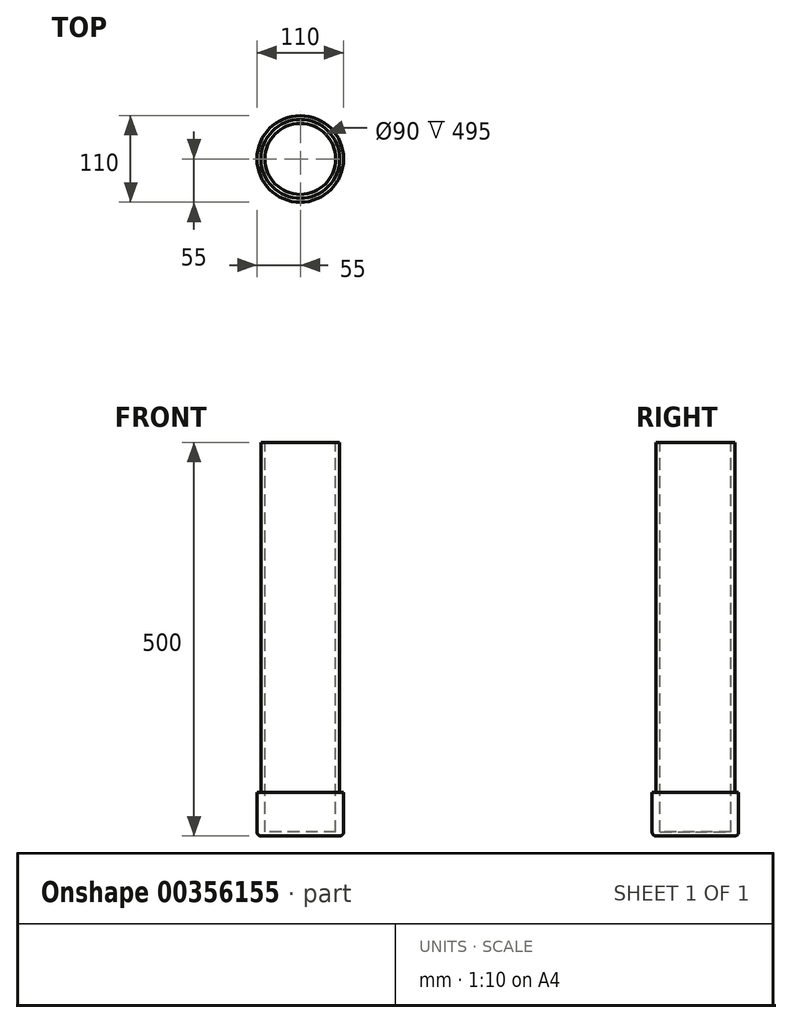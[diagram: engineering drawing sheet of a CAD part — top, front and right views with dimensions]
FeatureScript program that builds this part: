
annotation { "Feature Type Name" : "Feature", "Feature Type Description" : "" }
export const myFeature = defineFeature(function(context is Context, id is Id, definition is map)
    precondition{}
    {
        {
            var Q0;
            Q0=qCreatedBy(makeId("Front.planeOp"),FACE);
            var sketch = newSketch(context, id + "F0", { "sketchPlane" : qUnion([Q0])});
            skLineSegment(sketch, "E0.bottom", {"start": v(0, 0) * mm, "end": v(-50, 0) * mm});
            skLineSegment(sketch, "E0.top", {"start": v(0, 500) * mm, "end": v(-50, 500) * mm});
            skLineSegment(sketch, "E0.left", {"start": v(0, 0) * mm, "end": v(0, 500) * mm});
            skLineSegment(sketch, "E0.right", {"start": v(-50, 0) * mm, "end": v(-50, 500) * mm});
            skLineSegment(sketch, "E1.bottom", {"start": v(-50, 0) * mm, "end": v(-50, 0) * mm});
            skLineSegment(sketch, "E1.top", {"start": v(-50, 55) * mm, "end": v(-55, 55) * mm});
            skLineSegment(sketch, "E1.left", {"start": v(-50, 0) * mm, "end": v(-50, 55) * mm});
            skLineSegment(sketch, "E1.right", {"start": v(-55, 5) * mm, "end": v(-55, 55) * mm});
            skLineSegment(sketch, "E2.bottom", {"start": v(0, 500) * mm, "end": v(-45, 500) * mm});
            skLineSegment(sketch, "E2.top", {"start": v(0, 5) * mm, "end": v(-45, 5) * mm});
            skLineSegment(sketch, "E2.left", {"start": v(0, 500) * mm, "end": v(0, 5) * mm});
            skLineSegment(sketch, "E2.right", {"start": v(-45, 500) * mm, "end": v(-45, 5) * mm});
            skPoint(sketch, "E3.visualSharp", {"position": v(-55, 0) * mm});
            skArc(sketch, "E3.filletArc", {"start": v(-55, 5) * mm, "mid": v(-53.54, 1.46) * mm, "end": v(-50, 0) * mm});
            skSolve(sketch);
        }
        {
            var Q0;
            Q0=makeQuery(id+"F0.imprint","IMPRINT",FACE,{"disambiguationData":[TD([[makeQuery(id+"F0.imprint","IMPRINT",EDGE,{"derivedFrom":sQuery(id+"F0.wireOp",EDGE,"E1.top")}),1.0]])]});
            var Q1;
            Q1=makeQuery(id+"F0.imprint","IMPRINT",FACE,{"disambiguationData":[TD([[makeQuery(id+"F0.imprint","IMPRINT",EDGE,{"derivedFrom":sQuery(id+"F0.wireOp",EDGE,"E0.bottom")}),-1.0]])]});
            var Q2;
            Q2=sQuery(id+"F0.wireOp",EDGE,"E2.left");
            revolve(context, id + "F1", {"entities" : qUnion([Q0, Q1]), "axis" : qUnion([Q2]), "revolveType" : RevolveType.FULL});
        }
    });
